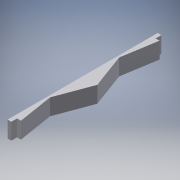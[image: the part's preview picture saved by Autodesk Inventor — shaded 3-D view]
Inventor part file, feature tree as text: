
AUTODESK INVENTOR PART (.ipt)
format: ipt  version: 2017 (Build 210142000, 142)  size: 122,368 bytes
history: native  units: in
note: dims shown in document units (in); Inventor stores cm internally (conversion verified against a paired STEP export)
features: extrude x3, sketch x3
ambient origin geometry x8: Origin, YZ Plane, XZ Plane, XY Plane, X Axis, Y Axis, Z Axis, Center Point
bodies: Solid1 (feature_tree)
feature tree (6):
  extrude  "Extrusion1"  Depth=0.134in
  sketch  "Sketch2"  dims[d2=0.134in d3=0.612in]
  extrude  "Extrusion2"  Depth=0.134in
  extrude  "Extrusion3"  Depth=0.065in
  sketch  "Sketch1"  dims[d0=2.436in d1=0.134in]
  sketch  "Sketch3"  dims[d4=1.223in d5=0.612in d6=0.035in d7=0.035in d8=0.2875in d9=0.0in d10=0.259in d12=0.065in d13=0.101in d14=0.0in d15=0.101in d16=0.0in d17=0.065in]
